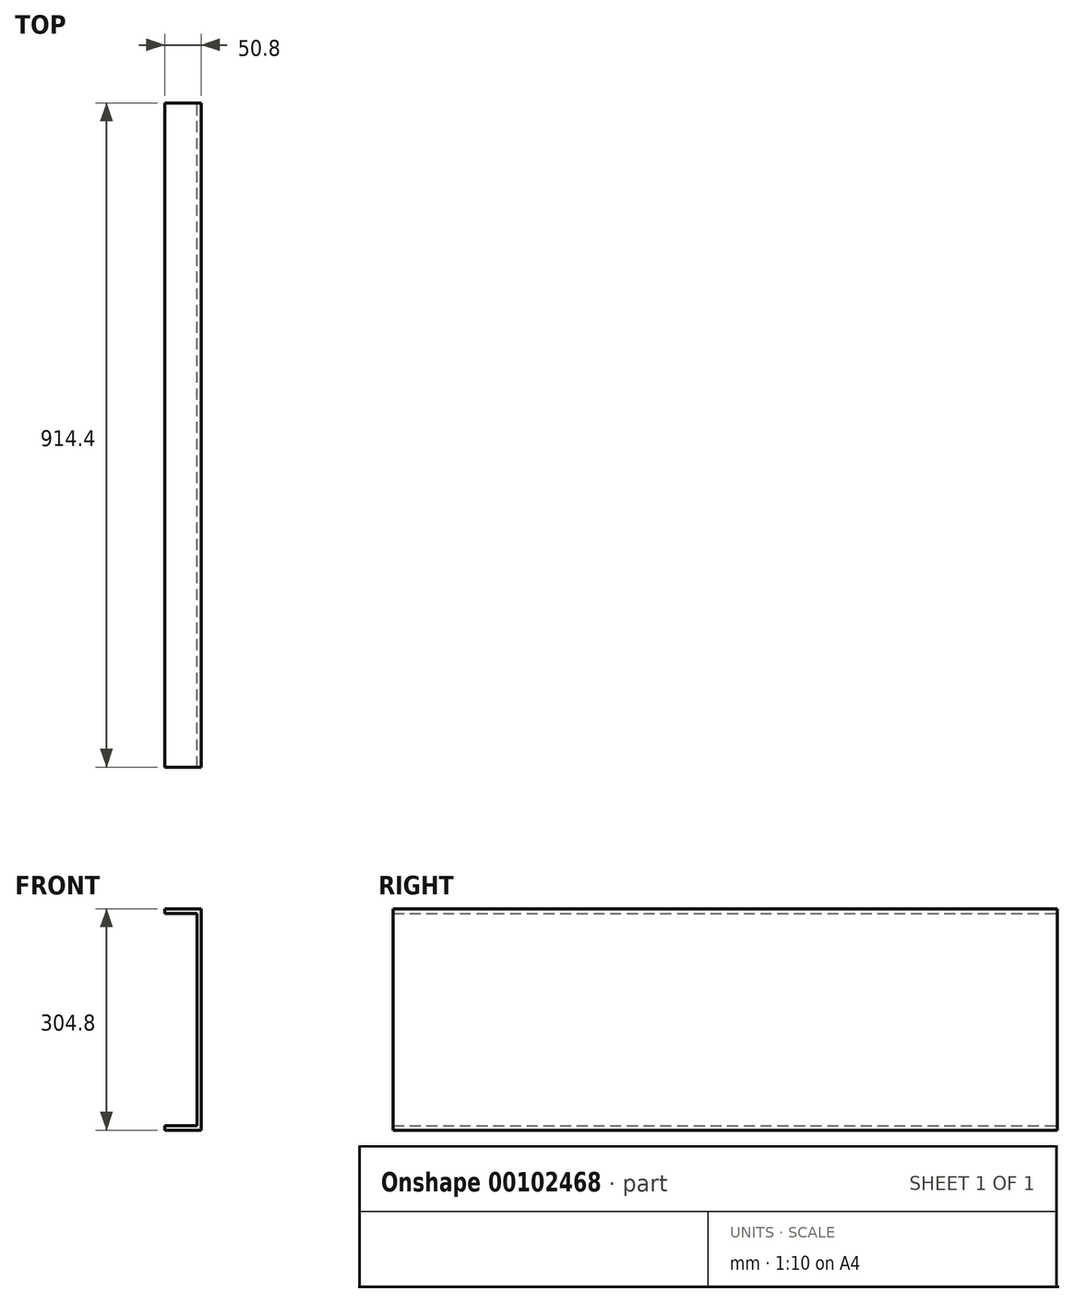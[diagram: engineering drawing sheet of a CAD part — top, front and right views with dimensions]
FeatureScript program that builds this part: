
annotation { "Feature Type Name" : "Feature", "Feature Type Description" : "" }
export const myFeature = defineFeature(function(context is Context, id is Id, definition is map)
    precondition{}
    {
        {
            var Q0;
            Q0=qCreatedBy(makeId("Front.planeOp"),FACE);
            var sketch = newSketch(context, id + "F0", { "sketchPlane" : qUnion([Q0])});
            skLineSegment(sketch, "E0", {"start": v(0, 180.98) * mm, "end": v(0, -123.82) * mm});
            skLineSegment(sketch, "E1", {"start": v(0, 180.98) * mm, "end": v(-50.8, 180.98) * mm});
            skLineSegment(sketch, "E2", {"start": v(0, -123.82) * mm, "end": v(-50.8, -123.82) * mm});
            skLineSegment(sketch, "E3.0", {"start": v(-6.35, 174.63) * mm, "end": v(-50.8, 174.63) * mm});
            skLineSegment(sketch, "E3.1", {"start": v(-6.35, 174.63) * mm, "end": v(-6.35, -117.48) * mm});
            skLineSegment(sketch, "E3.2", {"start": v(-6.35, -117.48) * mm, "end": v(-50.8, -117.48) * mm});
            skLineSegment(sketch, "E4", {"start": v(-50.8, 180.98) * mm, "end": v(-50.8, 174.63) * mm});
            skLineSegment(sketch, "E5", {"start": v(-50.8, -123.82) * mm, "end": v(-50.8, -117.48) * mm});
            skSolve(sketch);
        }
        {
            var Q0;
            Q0 = qSketchRegion(id + "F0", true);
            extrude(context, id + "F1", {"entities" : qUnion([Q0]), "depth" : 914.4 * mm});
        }
    });
